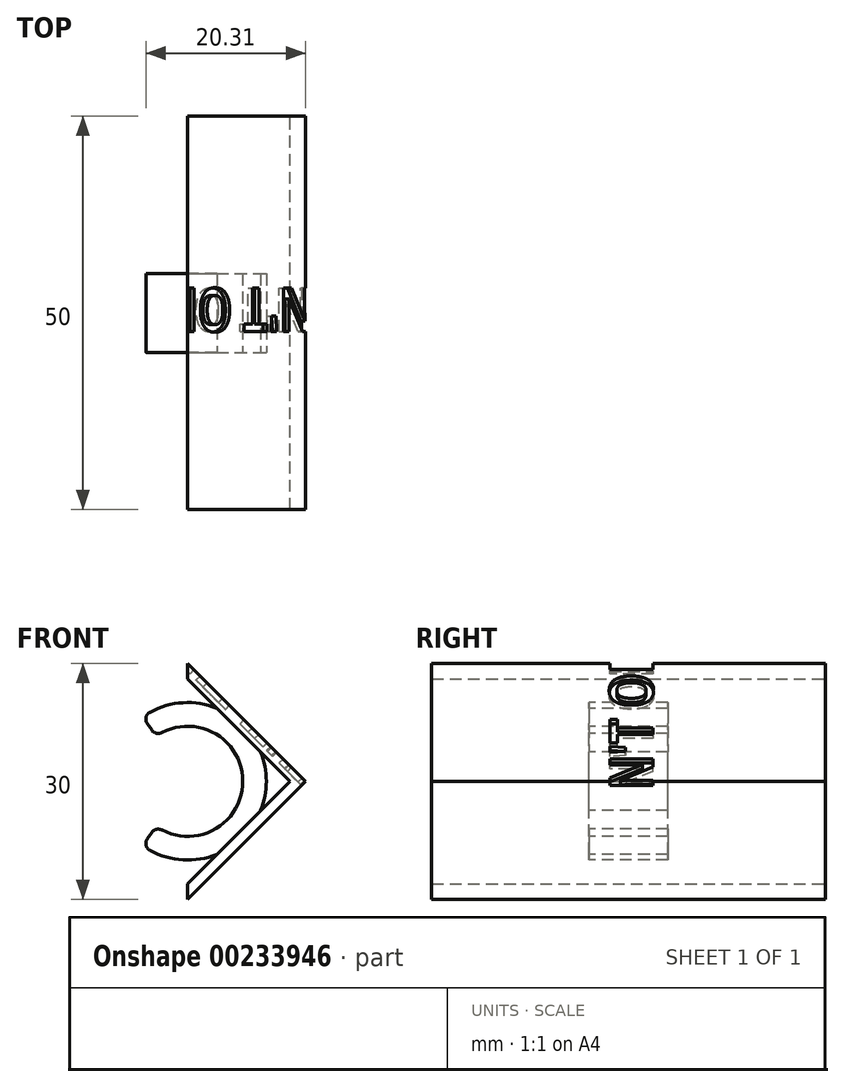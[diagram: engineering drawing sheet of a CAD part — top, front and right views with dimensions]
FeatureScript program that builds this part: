
annotation { "Feature Type Name" : "Feature", "Feature Type Description" : "" }
export const myFeature = defineFeature(function(context is Context, id is Id, definition is map)
    precondition{}
    {
        {
            var Q0;
            Q0=qCreatedBy(makeId("Front.planeOp"),FACE);
            var sketch = newSketch(context, id + "F0", { "sketchPlane" : qUnion([Q0])});
            skArc(sketch, "E0", {"start": v(-4.02, -5.73) * mm, "mid": v(7, 0) * mm, "end": v(-4.02, 5.73) * mm});
            skArc(sketch, "E1", {"start": v(-5.74, -8.2) * mm, "mid": v(10, 0) * mm, "end": v(-5.74, 8.2) * mm});
            skLineSegment(sketch, "E2", {"start": v(-4.02, -5.73) * mm, "end": v(-5.74, -8.2) * mm});
            skLineSegment(sketch, "E3", {"start": v(-4.02, 5.73) * mm, "end": v(-5.74, 8.2) * mm});
            skSolve(sketch);
        }
        {
            var Q0;
            Q0=makeQuery(id+"F0.imprint","IMPRINT",FACE,{"disambiguationData":[TD([[makeQuery(id+"F0.imprint","IMPRINT",EDGE,{"derivedFrom":sQuery(id+"F0.wireOp",EDGE,"E0")}),-1.0]])]});
            extrude(context, id + "F1", {"entities" : qUnion([Q0]), "endBound" : BoundingType.SYMMETRIC, "oppositeDirection" : true, "depth" : 10 * mm});
        }
        {
            var Q0;
            Q0=qCreatedBy(makeId("Front.planeOp"),FACE);
            var sketch = newSketch(context, id + "F2", { "sketchPlane" : qUnion([Q0])});
            skLineSegment(sketch, "E4", {"start": v(13, 0) * mm, "end": v(0, 13) * mm});
            skLineSegment(sketch, "E5", {"start": v(13, 0) * mm, "end": v(0, -13) * mm});
            skLineSegment(sketch, "E6", {"start": v(0, 13) * mm, "end": v(0, 15) * mm});
            skLineSegment(sketch, "E7", {"start": v(0, 15) * mm, "end": v(15, 0) * mm});
            skLineSegment(sketch, "E8", {"start": v(15, 0) * mm, "end": v(0, -15) * mm});
            skLineSegment(sketch, "E9", {"start": v(0, -15) * mm, "end": v(0, -13) * mm});
            skSolve(sketch);
        }
        {
            var Q0;
            Q0=makeQuery(id+"F2.imprint","IMPRINT",FACE,{"disambiguationData":[TD([[makeQuery(id+"F2.imprint","IMPRINT",EDGE,{"derivedFrom":sQuery(id+"F2.wireOp",EDGE,"E4")}),-1.0]])]});
            extrude(context, id + "F3", {"entities" : qUnion([Q0]), "operationType" : NewBodyOperationType.ADD, "endBound" : BoundingType.SYMMETRIC, "depth" : 50 * mm});
        }
        {
            var Q0;
            Q0=makeQuery(id+"F3.opExtrude","SWEPT_FACE",FACE,{"disambiguationData":[OSD([sQuery(id+"F2.wireOp",EDGE,"E7")])]});
            var sketch = newSketch(context, id + "F4", { "sketchPlane" : qUnion([Q0])});
            skText(sketch, "E10", { "text": "DON\'T OPEN", "fontName": "OpenSans-Bold.ttf"});
            const initialGuessF4  = {"E10": [0.00313, -0.024, 0, 1, 0.00555]};
            skSetInitialGuess(sketch, initialGuessF4);
            skSolve(sketch);
        }
        {
            var Q0;
            Q0 = qSketchRegion(id + "F4", true);
            extrude(context, id + "F5", {"entities" : qUnion([Q0]), "operationType" : NewBodyOperationType.REMOVE, "oppositeDirection" : true, "depth" : .75 * mm});
        }
        {
            var Q0;
            Q0=makeQuery(id+"F1.opExtrude","SWEPT_EDGE",EDGE,{"disambiguationData":[OSD([sQuery(id+"F0.wireOp",EDGE,"E0"),sQuery(id+"F0.wireOp",EDGE,"E3")])]});
            var Q1;
            Q1=makeQuery(id+"F1.opExtrude","SWEPT_EDGE",EDGE,{"disambiguationData":[OSD([sQuery(id+"F0.wireOp",EDGE,"E1"),sQuery(id+"F0.wireOp",EDGE,"E3")])]});
            var Q2;
            Q2=makeQuery(id+"F1.opExtrude","SWEPT_EDGE",EDGE,{"disambiguationData":[OSD([sQuery(id+"F0.wireOp",EDGE,"E0"),sQuery(id+"F0.wireOp",EDGE,"E2")])]});
            var Q3;
            Q3=makeQuery(id+"F1.opExtrude","SWEPT_EDGE",EDGE,{"disambiguationData":[OSD([sQuery(id+"F0.wireOp",EDGE,"E1"),sQuery(id+"F0.wireOp",EDGE,"E2")])]});
            fillet(context, id + "F6", {"entities" : qUnion([Q0, Q1, Q2, Q3]), "radius" : 1 * mm, "tangentPropagation" : true, "allowEdgeOverflow" : false});
        }
    });
